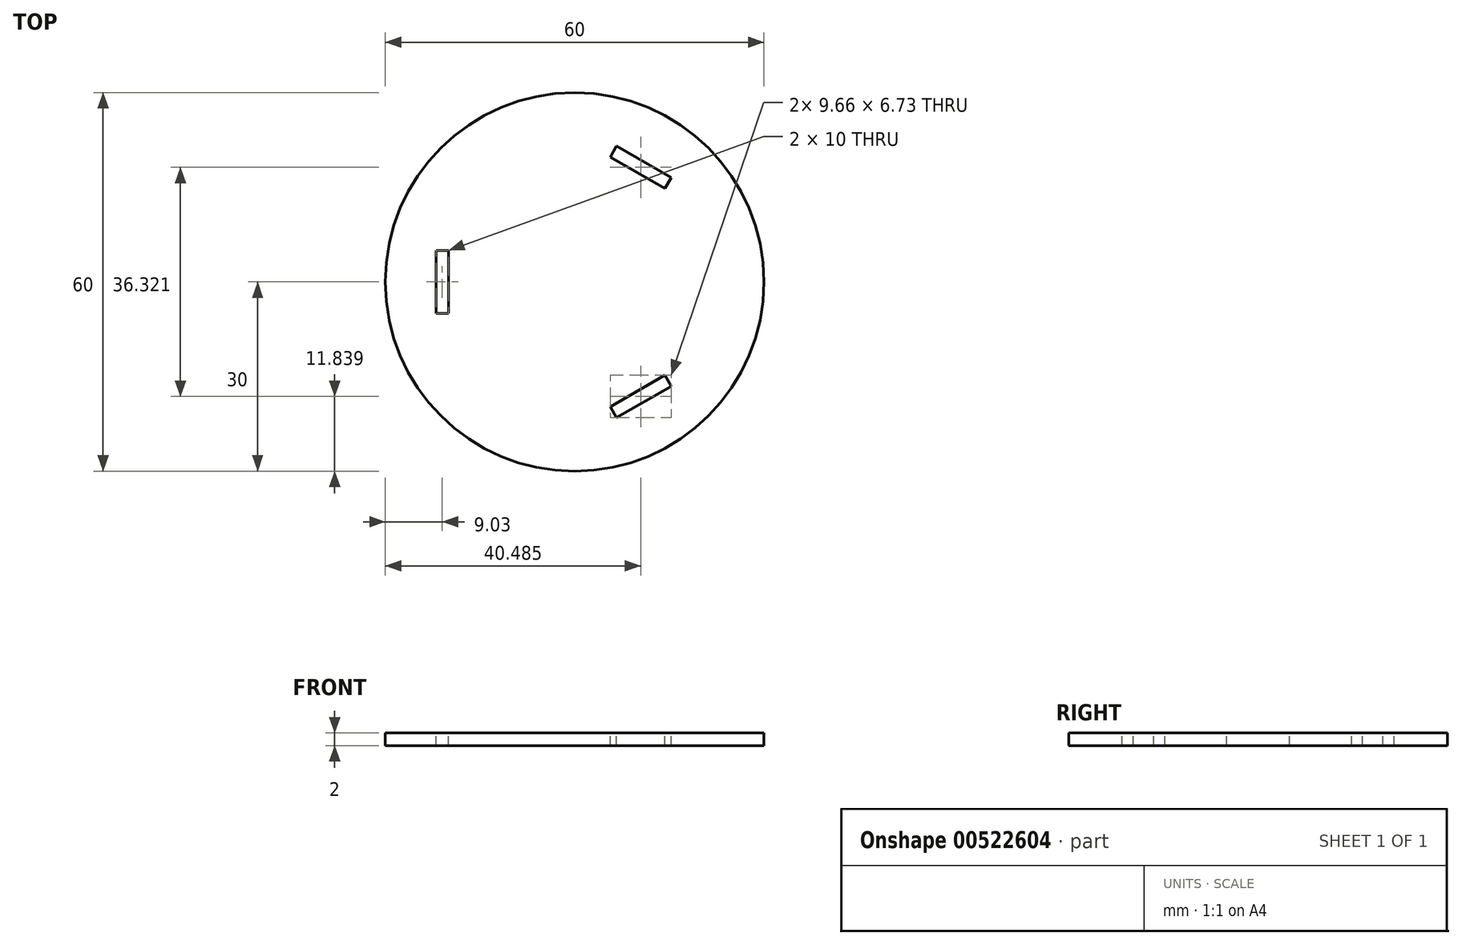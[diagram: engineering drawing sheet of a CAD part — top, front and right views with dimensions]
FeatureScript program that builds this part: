
annotation { "Feature Type Name" : "Feature", "Feature Type Description" : "" }
export const myFeature = defineFeature(function(context is Context, id is Id, definition is map)
    precondition{}
    {
        {
            var Q0;
            Q0=qCreatedBy(makeId("Top.planeOp"),FACE);
            var sketch = newSketch(context, id + "F0", { "sketchPlane" : qUnion([Q0])});
            skCircle(sketch, "E0", {"center": v(0, 0) * mm, "radius": 30 * mm});
            skSolve(sketch);
        }
        {
            var Q0;
            Q0 = qSketchRegion(id + "F0", true);
            extrude(context, id + "F1", {"entities" : qUnion([Q0]), "depth" : 2 * mm, "offsetDistance" : 25 * mm});
        }
        {
            var Q0;
            Q0=makeQuery(id+"F1.opExtrude","CAP_FACE",FACE,{"disambiguationData":[OSD([sQuery(id+"F0.wireOp",EDGE,"E0")])],"isStart":false});
            var sketch = newSketch(context, id + "F2", { "sketchPlane" : qUnion([Q0])});
            skLineSegment(sketch, "E1.bottom", {"start": v(-21.97, 5) * mm, "end": v(-19.97, 5) * mm});
            skLineSegment(sketch, "E1.top", {"start": v(-21.97, -5) * mm, "end": v(-19.97, -5) * mm});
            skLineSegment(sketch, "E1.left", {"start": v(-21.97, 5) * mm, "end": v(-21.97, -5) * mm});
            skLineSegment(sketch, "E1.right", {"start": v(-19.97, 5) * mm, "end": v(-19.97, -5) * mm});
            skSolve(sketch);
        }
        {
            var Q0;
            Q0=makeQuery(id+"F2.imprint","IMPRINT",FACE,{"disambiguationData":[TD([[makeQuery(id+"F2.imprint","IMPRINT",EDGE,{"derivedFrom":sQuery(id+"F2.wireOp",EDGE,"E1.bottom")}),-1.0]])]});
            extrude(context, id + "F3", {"entities" : qUnion([Q0]), "depth" : 25 * mm, "offsetDistance" : 25 * mm});
        }
        {
            var Q0;
            Q0=makeQuery(id+"F3.opExtrude","SWEPT_BODY",BODY,{"disambiguationData":[OSD([sQuery(id+"F2.wireOp",EDGE,"E1.bottom"),sQuery(id+"F2.wireOp",EDGE,"E1.top"),sQuery(id+"F2.wireOp",EDGE,"E1.left"),sQuery(id+"F2.wireOp",EDGE,"E1.right")])]});
            var Q1;
            Q1=makeQuery(id+"F1.opExtrude","SWEPT_FACE",FACE,{"disambiguationData":[OSD([sQuery(id+"F0.wireOp",EDGE,"E0")])]});
            circularPattern(context, id + "F4", {"entities" : qUnion([Q0]), "axis" : qUnion([Q1]), "angle" : 360 * degree, "instanceCount" : 3, "equalSpace" : true});
        }
        {
            var Q0;
            Q0=makeQuery(id+"F4.opPattern","COPY",FACE,{"derivedFrom":makeQuery(id+"F3.opExtrude","CAP_FACE",FACE,{"disambiguationData":[OSD([sQuery(id+"F2.wireOp",EDGE,"E1.bottom"),sQuery(id+"F2.wireOp",EDGE,"E1.top"),sQuery(id+"F2.wireOp",EDGE,"E1.left"),sQuery(id+"F2.wireOp",EDGE,"E1.right")])],"isStart":true}),"instanceName":"2"});
            var Q1;
            Q1=makeQuery(id+"F4.opPattern","COPY",FACE,{"derivedFrom":makeQuery(id+"F3.opExtrude","CAP_FACE",FACE,{"disambiguationData":[OSD([sQuery(id+"F2.wireOp",EDGE,"E1.bottom"),sQuery(id+"F2.wireOp",EDGE,"E1.top"),sQuery(id+"F2.wireOp",EDGE,"E1.left"),sQuery(id+"F2.wireOp",EDGE,"E1.right")])],"isStart":true}),"instanceName":"1"});
            var Q2;
            Q2=makeQuery(id+"F3.opExtrude","CAP_FACE",FACE,{"disambiguationData":[OSD([sQuery(id+"F2.wireOp",EDGE,"E1.bottom"),sQuery(id+"F2.wireOp",EDGE,"E1.top"),sQuery(id+"F2.wireOp",EDGE,"E1.left"),sQuery(id+"F2.wireOp",EDGE,"E1.right")])],"isStart":true});
            extrude(context, id + "F5", {"entities" : qUnion([Q0, Q1, Q2]), "operationType" : NewBodyOperationType.REMOVE, "depth" : 25 * mm, "offsetDistance" : 25 * mm});
        }
        {
            var Q0;
            Q0=makeQuery(id+"F3.opExtrude","CAP_FACE",FACE,{"disambiguationData":[OSD([sQuery(id+"F2.wireOp",EDGE,"E1.bottom"),sQuery(id+"F2.wireOp",EDGE,"E1.top"),sQuery(id+"F2.wireOp",EDGE,"E1.left"),sQuery(id+"F2.wireOp",EDGE,"E1.right")])],"isStart":true});
            var Q1;
            Q1=makeQuery(id+"F4.opPattern","COPY",FACE,{"derivedFrom":makeQuery(id+"F3.opExtrude","CAP_FACE",FACE,{"disambiguationData":[OSD([sQuery(id+"F2.wireOp",EDGE,"E1.bottom"),sQuery(id+"F2.wireOp",EDGE,"E1.top"),sQuery(id+"F2.wireOp",EDGE,"E1.left"),sQuery(id+"F2.wireOp",EDGE,"E1.right")])],"isStart":true}),"instanceName":"1"});
            var Q2;
            Q2=makeQuery(id+"F4.opPattern","COPY",FACE,{"derivedFrom":makeQuery(id+"F3.opExtrude","CAP_FACE",FACE,{"disambiguationData":[OSD([sQuery(id+"F2.wireOp",EDGE,"E1.bottom"),sQuery(id+"F2.wireOp",EDGE,"E1.top"),sQuery(id+"F2.wireOp",EDGE,"E1.left"),sQuery(id+"F2.wireOp",EDGE,"E1.right")])],"isStart":true}),"instanceName":"2"});
            extrude(context, id + "F6", {"entities" : qUnion([Q0, Q1, Q2]), "operationType" : NewBodyOperationType.REMOVE, "oppositeDirection" : true, "depth" : 25 * mm, "offsetDistance" : 25 * mm});
        }
    });
